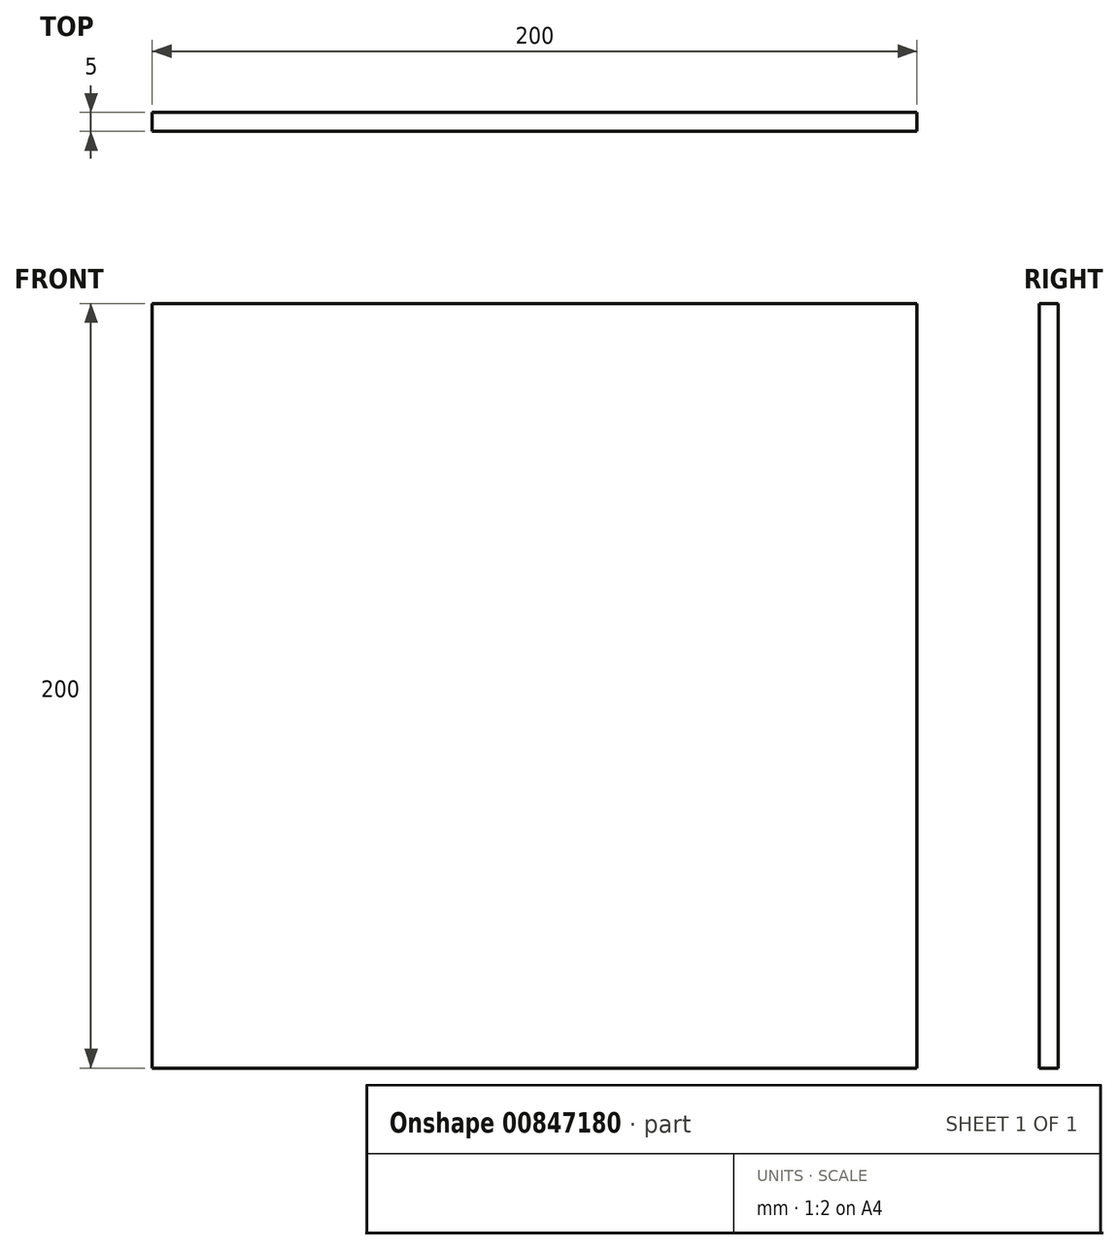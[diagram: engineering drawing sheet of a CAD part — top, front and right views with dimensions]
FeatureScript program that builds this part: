
annotation { "Feature Type Name" : "Feature", "Feature Type Description" : "" }
export const myFeature = defineFeature(function(context is Context, id is Id, definition is map)
    precondition{}
    {
        {
            var Q0;
            Q0=qCreatedBy(makeId("Front.planeOp"),FACE);
            var sketch = newSketch(context, id + "F0", { "sketchPlane" : qUnion([Q0])});
            skLineSegment(sketch, "E0.bottom", {"start": v(0, 0) * mm, "end": v(-200, 0) * mm});
            skLineSegment(sketch, "E0.top", {"start": v(0, -200) * mm, "end": v(-200, -200) * mm});
            skLineSegment(sketch, "E0.left", {"start": v(0, 0) * mm, "end": v(0, -200) * mm});
            skLineSegment(sketch, "E0.right", {"start": v(-200, 0) * mm, "end": v(-200, -200) * mm});
            skSolve(sketch);
        }
        {
            var Q0;
            Q0=makeQuery(id+"F0.imprint","IMPRINT",FACE,{"disambiguationData":[TD([[makeQuery(id+"F0.imprint","IMPRINT",EDGE,{"derivedFrom":sQuery(id+"F0.wireOp",EDGE,"E0.bottom")}),1.0]])]});
            extrude(context, id + "F1", {"entities" : qUnion([Q0]), "depth" : 5 * mm, "offsetDistance" : 25 * mm});
        }
    });
